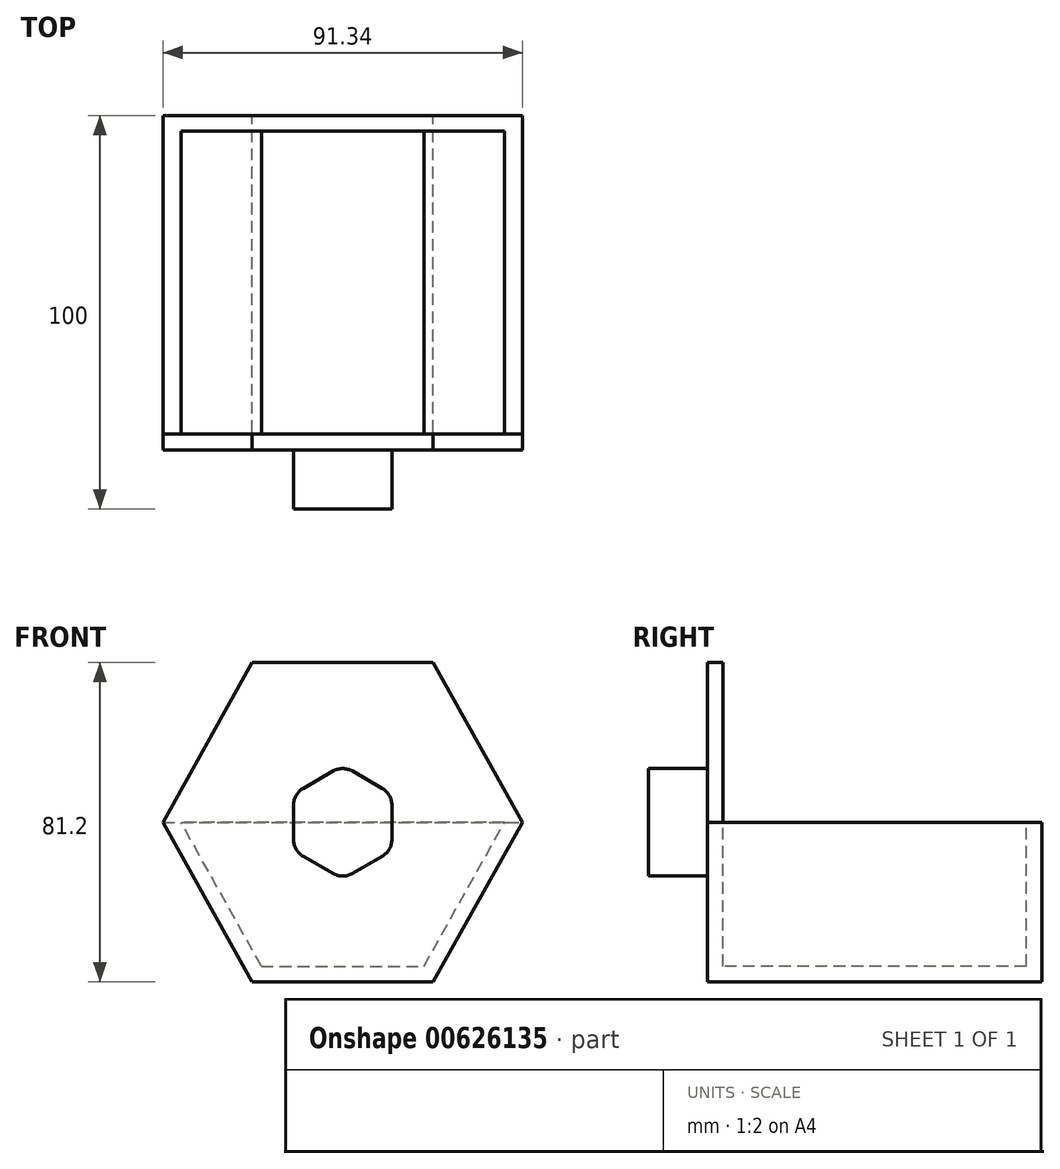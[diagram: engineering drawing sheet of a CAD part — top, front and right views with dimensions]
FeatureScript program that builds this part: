
annotation { "Feature Type Name" : "Feature", "Feature Type Description" : "" }
export const myFeature = defineFeature(function(context is Context, id is Id, definition is map)
    precondition{}
    {
        {
            var Q0;
            Q0=qCreatedBy(makeId("Front.planeOp"),FACE);
            var sketch = newSketch(context, id + "F0", { "sketchPlane" : qUnion([Q0])});
            skLineSegment(sketch, "E0", {"start": v(0, 0) * mm, "end": v(46, 0) * mm});
            skLineSegment(sketch, "E1", {"start": v(46, 0) * mm, "end": v(68.67, 40.6) * mm});
            skLineSegment(sketch, "E2", {"start": v(23, 0) * mm, "end": v(23, 13.5) * mm});
            skLineSegment(sketch, "E3.MirrorCS", {"start": v(0, 0) * mm, "end": v(-22.67, 40.6) * mm});
            skLineSegment(sketch, "E4", {"start": v(-22.67, 40.6) * mm, "end": v(-14.36, 40.6) * mm});
            skLineSegment(sketch, "E5.MirrorCS", {"start": v(0, 81.2) * mm, "end": v(46, 81.2) * mm});
            skLineSegment(sketch, "E6.MirrorCS", {"start": v(46, 81.2) * mm, "end": v(68.67, 40.6) * mm});
            skLineSegment(sketch, "E7.MirrorCS", {"start": v(0, 81.2) * mm, "end": v(-22.67, 40.6) * mm});
            skSolve(sketch);
        }
        {
            var Q0;
            Q0 = qSketchRegion(id + "F0", true);
            extrude(context, id + "F1", {"entities" : qUnion([Q0]), "depth" : 4 * mm, "offsetDistance" : 25 * mm});
        }
        {
            var Q0;
            Q0=makeQuery(id+"F1.opExtrude","CAP_FACE",FACE,{"disambiguationData":[OSD([sQuery(id+"F0.wireOp",EDGE,"E0"),sQuery(id+"F0.wireOp",EDGE,"E1"),sQuery(id+"F0.wireOp",EDGE,"b4b5bcd6-27cc-4902-85a2-76948127a4990.MirrorCS"),sQuery(id+"F0.wireOp",EDGE,"36ef5a83-e39f-40ad-bc1a-6a3bdd8d43e60.MirrorCS"),sQuery(id+"F0.wireOp",EDGE,"2137b016-2f0e-40ac-abac-8fcf89ab35ac0.MirrorCS"),sQuery(id+"F0.wireOp",EDGE,"b63468d8-efa5-4967-aad3-34c4b6585e060.MirrorCS")])],"isStart":false});
            var sketch = newSketch(context, id + "F2", { "sketchPlane" : qUnion([Q0])});
            skCircle(sketch, "E8", {"center": v(23, 40.6) * mm, "radius": 12.5 * mm});
            skCircle(sketch, "E9.cCircle", {"center": v(23, 40.6) * mm, "radius": 12.5 * mm, "construction": true});
            skLineSegment(sketch, "E9.0", {"start": v(35.5, 47.82) * mm, "end": v(35.5, 33.38) * mm});
            skLineSegment(sketch, "E9.1", {"start": v(35.5, 33.38) * mm, "end": v(23, 26.17) * mm});
            skLineSegment(sketch, "E9.2", {"start": v(23, 26.17) * mm, "end": v(10.5, 33.38) * mm});
            skLineSegment(sketch, "E9.3", {"start": v(10.5, 33.38) * mm, "end": v(10.5, 47.82) * mm});
            skLineSegment(sketch, "E9.4", {"start": v(10.5, 47.82) * mm, "end": v(23, 55.03) * mm});
            skLineSegment(sketch, "E9.5", {"start": v(23, 55.03) * mm, "end": v(35.5, 47.82) * mm});
            skPoint(sketch, "E9.0.midPoint", {"position": v(35.5, 40.6) * mm});
            skSolve(sketch);
        }
        {
            var Q0;
            Q0 = qSketchRegion(id + "F2", true);
            extrude(context, id + "F3", {"entities" : qUnion([Q0]), "operationType" : NewBodyOperationType.ADD, "depth" : 15 * mm, "offsetDistance" : 25 * mm});
        }
        {
            var Q0;
            Q0=makeQuery(id+"F3.opExtrude","SWEPT_EDGE",EDGE,{"disambiguationData":[OSD([sQuery(id+"F2.wireOp",EDGE,"E9.0"),sQuery(id+"F2.wireOp",EDGE,"E9.5")])]});
            var Q1;
            Q1=makeQuery(id+"F3.opExtrude","SWEPT_EDGE",EDGE,{"disambiguationData":[OSD([sQuery(id+"F2.wireOp",EDGE,"E9.4"),sQuery(id+"F2.wireOp",EDGE,"E9.5")])]});
            var Q2;
            Q2=makeQuery(id+"F3.opExtrude","SWEPT_EDGE",EDGE,{"disambiguationData":[OSD([sQuery(id+"F2.wireOp",EDGE,"E9.3"),sQuery(id+"F2.wireOp",EDGE,"E9.4")])]});
            var Q3;
            Q3=makeQuery(id+"F3.opExtrude","SWEPT_EDGE",EDGE,{"disambiguationData":[OSD([sQuery(id+"F2.wireOp",EDGE,"E9.0"),sQuery(id+"F2.wireOp",EDGE,"E9.1")])]});
            var Q4;
            Q4=makeQuery(id+"F3.opExtrude","SWEPT_EDGE",EDGE,{"disambiguationData":[OSD([sQuery(id+"F2.wireOp",EDGE,"E9.1"),sQuery(id+"F2.wireOp",EDGE,"E9.2")])]});
            var Q5;
            Q5=makeQuery(id+"F3.opExtrude","SWEPT_EDGE",EDGE,{"disambiguationData":[OSD([sQuery(id+"F2.wireOp",EDGE,"E9.2"),sQuery(id+"F2.wireOp",EDGE,"E9.3")])]});
            fillet(context, id + "F4", {"entities" : qUnion([Q0, Q1, Q2, Q3, Q4, Q5]), "radius" : 5 * mm, "tangentPropagation" : true, "allowEdgeOverflow" : false});
        }
        {
            var Q0;
            Q0=makeQuery(id+"F1.opExtrude","CAP_FACE",FACE,{"disambiguationData":[OSD([sQuery(id+"F0.wireOp",EDGE,"E0"),sQuery(id+"F0.wireOp",EDGE,"E1"),sQuery(id+"F0.wireOp",EDGE,"E3.MirrorCS"),sQuery(id+"F0.wireOp",EDGE,"E5.MirrorCS"),sQuery(id+"F0.wireOp",EDGE,"E6.MirrorCS"),sQuery(id+"F0.wireOp",EDGE,"E7.MirrorCS")])],"isStart":false});
            var sketch = newSketch(context, id + "F5", { "sketchPlane" : qUnion([Q0])});
            skLineSegment(sketch, "E10.0", {"start": v(43.65, 4) * mm, "end": v(65.18, 42.55) * mm});
            skLineSegment(sketch, "E10.1", {"start": v(2.35, 4) * mm, "end": v(43.65, 4) * mm});
            skLineSegment(sketch, "E10.2", {"start": v(2.35, 4) * mm, "end": v(-19.18, 42.55) * mm});
            skLineSegment(sketch, "E11", {"start": v(-22.67, 40.6) * mm, "end": v(68.67, 40.6) * mm});
            skLineSegment(sketch, "E12", {"start": v(-22.67, 40.6) * mm, "end": v(-2.26, 0) * mm});
            skLineSegment(sketch, "E13", {"start": v(-2.26, 0) * mm, "end": v(46, 0) * mm});
            skLineSegment(sketch, "E14", {"start": v(46, 0) * mm, "end": v(68.67, 40.6) * mm});
            skSolve(sketch);
        }
        {
            var Q0;
            {var subQ4=sQuery(id+"F5.wireOp",EDGE,"E10.1");Q0=makeQuery(id+"F5.imprint","IMPRINT",FACE,{"disambiguationData":[TD([[makeQuery(id+"F5.imprint","IMPRINT",EDGE,{"derivedFrom":subQ4}),-1.0]])]});}
            extrude(context, id + "F6", {"entities" : qUnion([Q0]), "operationType" : NewBodyOperationType.ADD, "oppositeDirection" : true, "depth" : 85 * mm, "offsetDistance" : 25 * mm});
        }
        {
            var Q0;
            Q0=makeQuery(id+"F6.opExtrude","CAP_FACE",FACE,{"disambiguationData":[OSD([sQuery(id+"F0.wireOp",EDGE,"E3.MirrorCS"),sQuery(id+"F5.wireOp",EDGE,"E10.0"),sQuery(id+"F5.wireOp",EDGE,"E10.1"),sQuery(id+"F5.wireOp",EDGE,"E10.2"),sQuery(id+"F5.wireOp",EDGE,"E11"),sQuery(id+"F5.wireOp",EDGE,"E13"),sQuery(id+"F5.wireOp",EDGE,"E14")])],"isStart":false});
            var sketch = newSketch(context, id + "F7", { "sketchPlane" : qUnion([Q0])});
            skLineSegment(sketch, "E15", {"start": v(-68.67, 40.6) * mm, "end": v(22.67, 40.6) * mm});
            skLineSegment(sketch, "E16", {"start": v(22.67, 40.6) * mm, "end": v(0, 0) * mm});
            skLineSegment(sketch, "E17", {"start": v(0, 0) * mm, "end": v(-46, 0) * mm});
            skLineSegment(sketch, "E18", {"start": v(-46, 0) * mm, "end": v(-68.67, 40.6) * mm});
            skSolve(sketch);
        }
        {
            var Q0;
            Q0 = qSketchRegion(id + "F7", true);
            extrude(context, id + "F8", {"entities" : qUnion([Q0]), "operationType" : NewBodyOperationType.ADD, "oppositeDirection" : true, "depth" : 4 * mm, "offsetDistance" : 25 * mm});
        }
    });
